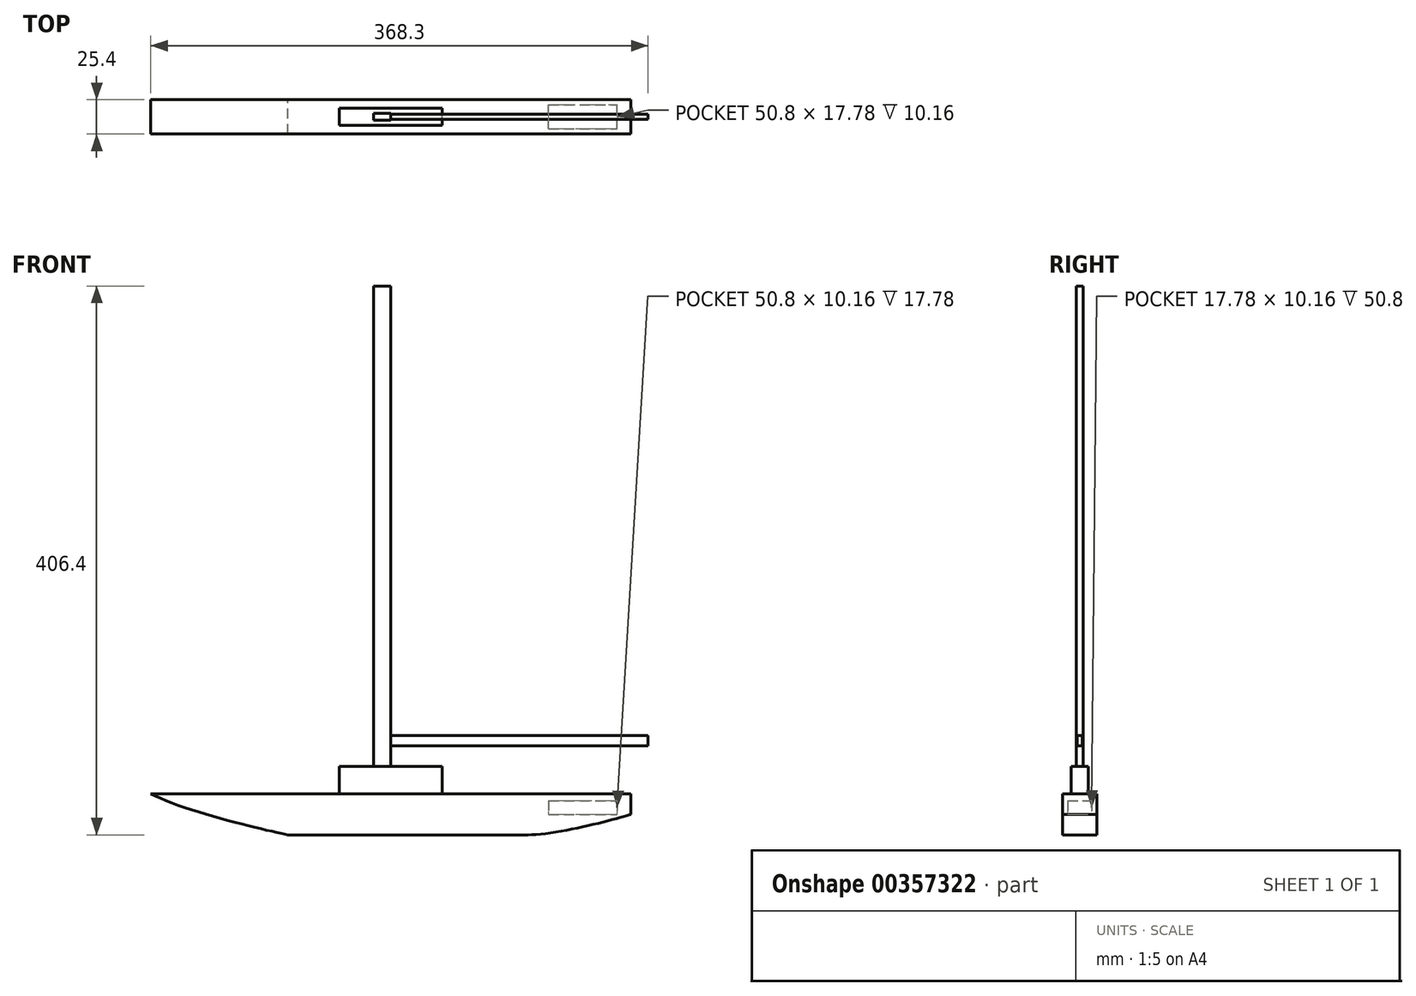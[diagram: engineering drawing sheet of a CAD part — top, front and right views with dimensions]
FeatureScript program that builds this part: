
annotation { "Feature Type Name" : "Feature", "Feature Type Description" : "" }
export const myFeature = defineFeature(function(context is Context, id is Id, definition is map)
    precondition{}
    {
        {
            var Q0;
            Q0=qCreatedBy(makeId("Front.planeOp"),FACE);
            var sketch = newSketch(context, id + "F0", { "sketchPlane" : qUnion([Q0])});
            skLineSegment(sketch, "E0.bottom", {"start": v(114.3, 15.24) * mm, "end": v(-63.5, 15.24) * mm});
            skLineSegment(sketch, "E0.top", {"start": v(114.3, -15.24) * mm, "end": v(-63.5, -15.24) * mm});
            skLineSegment(sketch, "E0.left", {"start": v(114.3, 15.24) * mm, "end": v(114.3, -15.24) * mm});
            skLineSegment(sketch, "E0.right", {"start": v(-63.5, 15.24) * mm, "end": v(-63.5, -15.24) * mm});
            skLineSegment(sketch, "E1", {"start": v(-63.5, 15.24) * mm, "end": v(-165.1, 15.24) * mm});
            skLineSegment(sketch, "E2", {"start": v(114.3, 15.24) * mm, "end": v(190.5, 15.24) * mm});
            skLineSegment(sketch, "E3", {"start": v(190.5, 0) * mm, "end": v(190.5, 15.24) * mm});
            skFitSpline(sketch, "E4", {"points": [v(-165.1, 15.24) * mm, v(-63.5, -15.24) * mm], "startDerivative": vector(72.36, -39.1) * mm, "endDerivative": vector(46.48, -9.76) * mm});
            skFitSpline(sketch, "E5", {"points": [v(190.5, 0) * mm, v(114.3, -15.24) * mm], "startDerivative": vector(-30.68, -10.03) * mm, "endDerivative": vector(-64.36, -0.09) * mm});
            skLineSegment(sketch, "E6", {"start": v(-25.4, 15.24) * mm, "end": v(-25.4, 35.56) * mm});
            skLineSegment(sketch, "E7", {"start": v(0, 35.56) * mm, "end": v(0, 391.16) * mm});
            skLineSegment(sketch, "E8", {"start": v(0, 391.16) * mm, "end": v(12.7, 391.16) * mm});
            skLineSegment(sketch, "E9", {"start": v(12.7, 391.16) * mm, "end": v(12.7, 35.56) * mm});
            skLineSegment(sketch, "E10", {"start": v(12.7, 58.42) * mm, "end": v(203.2, 58.42) * mm});
            skLineSegment(sketch, "E11", {"start": v(203.2, 50.8) * mm, "end": v(203.2, 58.42) * mm});
            skLineSegment(sketch, "E12", {"start": v(203.2, 50.8) * mm, "end": v(12.7, 50.8) * mm});
            skLineSegment(sketch, "E13", {"start": v(-25.4, 35.56) * mm, "end": v(50.8, 35.56) * mm});
            skLineSegment(sketch, "E14", {"start": v(50.8, 35.56) * mm, "end": v(50.8, 15.24) * mm});
            skLineSegment(sketch, "E15", {"start": v(12.7, 35.56) * mm, "end": v(0, 35.56) * mm});
            skSolve(sketch);
        }
        {
            var Q0;
            Q0=makeQuery(id+"F0.imprint","IMPRINT",FACE,{"disambiguationData":[TD([[makeQuery(id+"F0.imprint","IMPRINT",EDGE,{"derivedFrom":sQuery(id+"F0.wireOp",EDGE,"E0.top")}),-1.0]])]});
            var Q1;
            Q1=makeQuery(id+"F0.imprint","IMPRINT",FACE,{"disambiguationData":[TD([[makeQuery(id+"F0.imprint","IMPRINT",EDGE,{"derivedFrom":sQuery(id+"F0.wireOp",EDGE,"E0.right")}),-1.0]])]});
            var Q2;
            {var subQ1=sQuery(id+"F0.wireOp",EDGE,"E0.left");Q2=makeQuery(id+"F0.imprint","IMPRINT",FACE,{"disambiguationData":[TD([[makeQuery(id+"F0.imprint","IMPRINT",EDGE,{"derivedFrom":subQ1}),1.0]])]});}
            extrude(context, id + "F1", {"entities" : qUnion([Q0, Q1, Q2]), "endBound" : BoundingType.SYMMETRIC, "depth" : 25.4 * mm});
        }
        {
            var Q0;
            {var subQ4=sQuery(id+"F0.wireOp",EDGE,"E7");Q0=makeQuery(id+"F0.imprint","IMPRINT",FACE,{"disambiguationData":[TD([[makeQuery(id+"F0.imprint","IMPRINT",EDGE,{"derivedFrom":subQ4}),-1.0]])]});}
            var Q1;
            {var subQ4=sQuery(id+"F0.wireOp",EDGE,"KWktz696-oDgb-sVVb-qTZQ-FjdrIhpwpodQ");Q1=makeQuery(id+"F0.imprint","IMPRINT",FACE,{"disambiguationData":[TD([[makeQuery(id+"F0.imprint","IMPRINT",EDGE,{"derivedFrom":subQ4}),1.0]])]});}
            extrude(context, id + "F2", {"entities" : qUnion([Q0, Q1]), "operationType" : NewBodyOperationType.ADD, "endBound" : BoundingType.SYMMETRIC, "depth" : 5.08 * mm});
        }
        {
            var Q0;
            {var subQ0=sQuery(id+"F0.wireOp",EDGE,"E10");Q0=makeQuery(id+"F0.imprint","IMPRINT",FACE,{"disambiguationData":[TD([[makeQuery(id+"F0.imprint","IMPRINT",EDGE,{"derivedFrom":subQ0}),-1.0]])]});}
            extrude(context, id + "F3", {"entities" : qUnion([Q0]), "operationType" : NewBodyOperationType.ADD, "endBound" : BoundingType.SYMMETRIC, "depth" : 3.8 * mm});
        }
        {
            var Q0;
            {var subQ3=sQuery(id+"F0.wireOp",EDGE,"E6");Q0=makeQuery(id+"F0.imprint","IMPRINT",FACE,{"disambiguationData":[TD([[makeQuery(id+"F0.imprint","IMPRINT",EDGE,{"derivedFrom":subQ3}),-1.0]])]});}
            extrude(context, id + "F4", {"entities" : qUnion([Q0]), "endBound" : BoundingType.SYMMETRIC, "depth" : 12.7 * mm});
        }
        {
            var Q0;
            Q0=qCreatedBy(makeId("Top.planeOp"),FACE);
            var sketch = newSketch(context, id + "F5", { "sketchPlane" : qUnion([Q0])});
            skLineSegment(sketch, "E16.bottom", {"start": v(129.54, -8.89) * mm, "end": v(180.34, -8.89) * mm});
            skLineSegment(sketch, "E16.top", {"start": v(129.54, 8.9) * mm, "end": v(180.34, 8.9) * mm});
            skLineSegment(sketch, "E16.left", {"start": v(129.54, -8.89) * mm, "end": v(129.54, 8.9) * mm});
            skLineSegment(sketch, "E16.right", {"start": v(180.34, -8.89) * mm, "end": v(180.34, 8.9) * mm});
            skPoint(sketch, "E16.middle", {"position": v(154.94, 0) * mm});
            skSolve(sketch);
        }
        {
            var Q0;
            Q0 = qSketchRegion(id + "F5", true);
            extrude(context, id + "F6", {"entities" : qUnion([Q0]), "operationType" : NewBodyOperationType.REMOVE, "depth" : 10.16 * mm});
        }
    });
